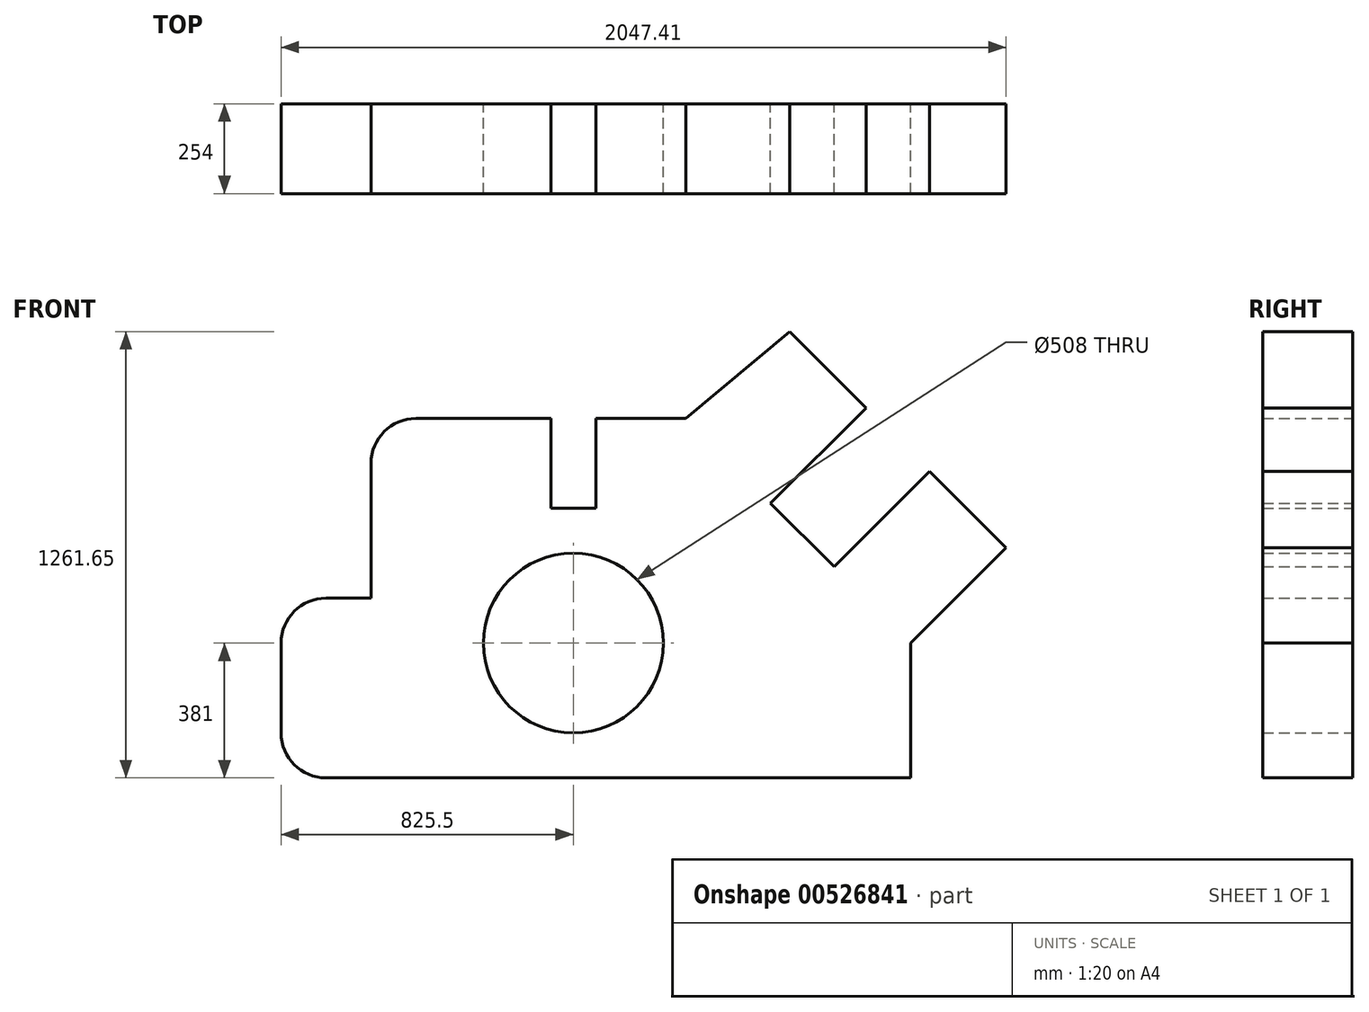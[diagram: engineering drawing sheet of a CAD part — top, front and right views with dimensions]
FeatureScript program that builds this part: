
annotation { "Feature Type Name" : "Feature", "Feature Type Description" : "" }
export const myFeature = defineFeature(function(context is Context, id is Id, definition is map)
    precondition{}
    {
        {
            var Q0;
            Q0=qCreatedBy(makeId("Front.planeOp"),FACE);
            var sketch = newSketch(context, id + "F0", { "sketchPlane" : qUnion([Q0])});
            skLineSegment(sketch, "E0", {"start": v(127, 0) * mm, "end": v(1778, 0) * mm});
            skLineSegment(sketch, "E1", {"start": v(1778, 0) * mm, "end": v(1778, 381) * mm});
            skLineSegment(sketch, "E2", {"start": v(0, 127) * mm, "end": v(0, 381) * mm});
            skPoint(sketch, "E3.visualSharp", {"position": v(0, 0) * mm});
            skArc(sketch, "E3.filletArc", {"start": v(0, 127) * mm, "mid": v(37.2, 37.2) * mm, "end": v(127, 0) * mm});
            skCircle(sketch, "E4", {"center": v(825.5, 381) * mm, "radius": 254 * mm});
            skLineSegment(sketch, "E5", {"start": v(127, 508) * mm, "end": v(254, 508) * mm});
            skLineSegment(sketch, "E6", {"start": v(254, 508) * mm, "end": v(254, 889) * mm});
            skLineSegment(sketch, "E7", {"start": v(381, 1016) * mm, "end": v(762, 1016) * mm});
            skLineSegment(sketch, "E8", {"start": v(762, 1016) * mm, "end": v(762, 762) * mm});
            skLineSegment(sketch, "E9", {"start": v(762, 762) * mm, "end": v(889, 762) * mm});
            skLineSegment(sketch, "E10", {"start": v(889, 762) * mm, "end": v(889, 1016) * mm});
            skLineSegment(sketch, "E11", {"start": v(889, 1016) * mm, "end": v(1143, 1016) * mm});
            skLineSegment(sketch, "E12", {"start": v(1778, 381) * mm, "end": v(2047.4, 650.4) * mm});
            skLineSegment(sketch, "E13", {"start": v(2047.4, 650.4) * mm, "end": v(1831.59, 866.23) * mm});
            skLineSegment(sketch, "E14", {"start": v(1831.59, 866.23) * mm, "end": v(1562.18, 596.82) * mm});
            skLineSegment(sketch, "E15", {"start": v(1562.18, 596.82) * mm, "end": v(1382.58, 776.42) * mm});
            skLineSegment(sketch, "E16", {"start": v(1382.58, 776.42) * mm, "end": v(1651.98, 1045.83) * mm});
            skLineSegment(sketch, "E17", {"start": v(1651.98, 1045.83) * mm, "end": v(1436.17, 1261.65) * mm});
            skPoint(sketch, "E18.visualSharp", {"position": v(0, 508) * mm});
            skArc(sketch, "E18.filletArc", {"start": v(127, 508) * mm, "mid": v(37.2, 470.8) * mm, "end": v(0, 381) * mm});
            skLineSegment(sketch, "E19", {"start": v(1143, 1016) * mm, "end": v(1436.17, 1261.65) * mm});
            skPoint(sketch, "E20.visualSharp", {"position": v(254, 1016) * mm});
            skArc(sketch, "E20.filletArc", {"start": v(381, 1016) * mm, "mid": v(291.2, 978.8) * mm, "end": v(254, 889) * mm});
            skSolve(sketch);
        }
        {
            var Q0;
            Q0 = qSketchRegion(id + "F0", true);
            extrude(context, id + "F1", {"entities" : qUnion([Q0]), "depth" : 254 * mm, "offsetDistance" : 25.4 * mm});
        }
    });
